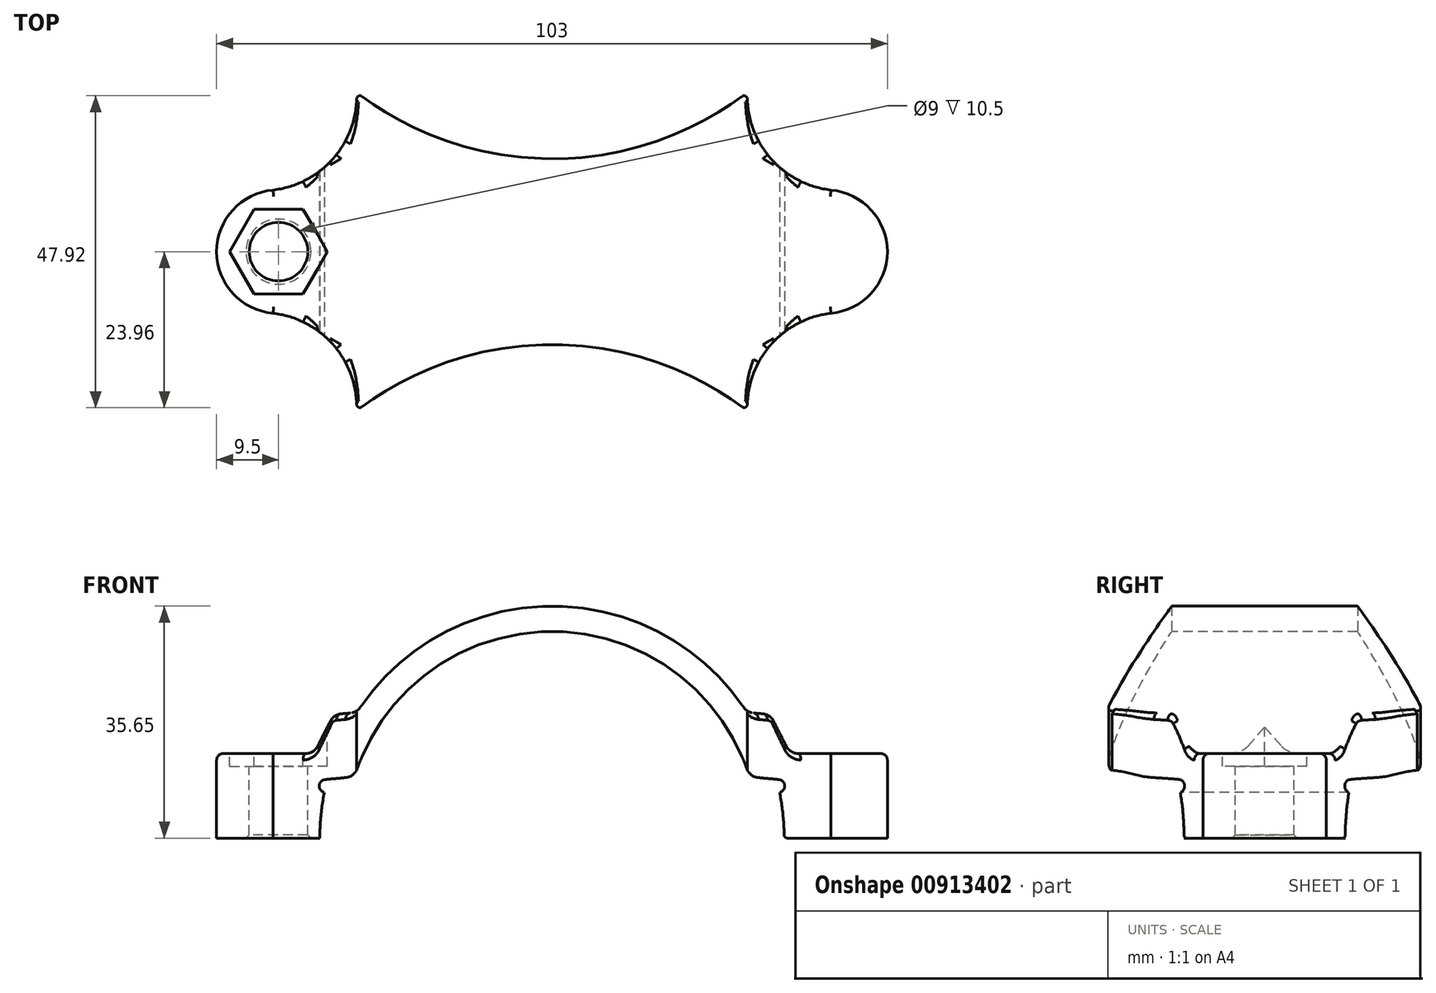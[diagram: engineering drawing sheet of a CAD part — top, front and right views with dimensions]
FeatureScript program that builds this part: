
annotation { "Feature Type Name" : "Feature", "Feature Type Description" : "" }
export const myFeature = defineFeature(function(context is Context, id is Id, definition is map)
    precondition{}
    {
        {
            var Q0;
            Q0=qCreatedBy(makeId("Top.planeOp"),FACE);
            var sketch = newSketch(context, id + "F0", { "sketchPlane" : qUnion([Q0])});
            skLineSegment(sketch, "E0", {"start": v(73.71, 0) * mm, "end": v(-77.72, 0) * mm, "construction": true});
            skLineSegment(sketch, "E1", {"start": v(0, 80.64) * mm, "end": v(0, -78.02) * mm, "construction": true});
            skLineSegment(sketch, "E2.0", {"start": v(42, 80.64) * mm, "end": v(42, -78.02) * mm, "construction": true});
            skArc(sketch, "E3", {"start": v(42.84, -9.46) * mm, "mid": v(51.5, 0) * mm, "end": v(42.84, 9.46) * mm});
            skLineSegment(sketch, "E4.0", {"start": v(29.5, 80.64) * mm, "end": v(29.5, -78.02) * mm, "construction": true});
            skArc(sketch, "E5", {"start": v(30, 23.46) * mm, "mid": v(29.73, 23.9) * mm, "end": v(29.2, 23.86) * mm});
            skPoint(sketch, "E6.first.point", {"position": v(30, 23.46) * mm});
            skArc(sketch, "E7.trimOffspring", {"start": v(30, 23.46) * mm, "mid": v(33.81, 14.06) * mm, "end": v(42.84, 9.46) * mm});
            skArc(sketch, "E8.MirrorCS", {"start": v(30, -23.46) * mm, "mid": v(33.81, -14.06) * mm, "end": v(42.84, -9.46) * mm});
            skArc(sketch, "E9.MirrorCS", {"start": v(30, -23.46) * mm, "mid": v(29.73, -23.9) * mm, "end": v(29.2, -23.86) * mm});
            skArc(sketch, "E10", {"start": v(-29.2, 23.86) * mm, "mid": v(0, 14.26) * mm, "end": v(29.2, 23.86) * mm});
            skArc(sketch, "E11.MirrorC", {"start": v(-29.2, -23.86) * mm, "mid": v(0, -14.26) * mm, "end": v(29.2, -23.86) * mm});
            skArc(sketch, "E12.MirrorCS", {"start": v(-30, 23.46) * mm, "mid": v(-29.73, 23.9) * mm, "end": v(-29.2, 23.86) * mm});
            skArc(sketch, "E13.MirrorCS", {"start": v(-30, 23.46) * mm, "mid": v(-33.81, 14.06) * mm, "end": v(-42.84, 9.46) * mm});
            skArc(sketch, "E14.MirrorC", {"start": v(-42.84, -9.46) * mm, "mid": v(-51.5, 0) * mm, "end": v(-42.84, 9.46) * mm});
            skArc(sketch, "E15.MirrorCS", {"start": v(-30, -23.46) * mm, "mid": v(-33.81, -14.06) * mm, "end": v(-42.84, -9.46) * mm});
            skArc(sketch, "E16.MirrorCS", {"start": v(-30, -23.46) * mm, "mid": v(-29.73, -23.9) * mm, "end": v(-29.2, -23.86) * mm});
            skPoint(sketch, "E17.orphan", {"position": v(29, -23.46) * mm});
            skPoint(sketch, "E18.orphan", {"position": v(-29, -23.46) * mm});
            skPoint(sketch, "E19.orphan", {"position": v(29, 23.46) * mm});
            skPoint(sketch, "E20.orphan", {"position": v(-29, 23.46) * mm});
            skSolve(sketch);
        }
        {
            var Q0;
            Q0=makeQuery(id+"F0.imprint","IMPRINT",FACE,{"disambiguationData":[TD([[makeQuery(id+"F0.imprint","IMPRINT",EDGE,{"derivedFrom":sQuery(id+"F0.wireOp",EDGE,"E3")}),1.0]])]});
            extrude(context, id + "F1", {"entities" : qUnion([Q0]), "depth" : 35.65 * mm, "offsetDistance" : 25 * mm});
        }
        {
            var Q0;
            Q0=qCreatedBy(makeId("Front.planeOp"),FACE);
            var sketch = newSketch(context, id + "F2", { "sketchPlane" : qUnion([Q0])});
            skLineSegment(sketch, "E21", {"start": v(75.28, 0) * mm, "end": v(-76.7, 0) * mm, "construction": true});
            skLineSegment(sketch, "E22", {"start": v(0, -8.46) * mm, "end": v(0, 103.78) * mm, "construction": true});
            skLineSegment(sketch, "E23.0", {"start": v(51.5, 13) * mm, "end": v(36.56, 13) * mm});
            skArc(sketch, "E24", {"start": v(30.32, 9.43) * mm, "mid": v(0, 31.75) * mm, "end": v(-30.32, 9.43) * mm});
            skArc(sketch, "E25", {"start": v(35.65, 0) * mm, "mid": v(35.47, 3.53) * mm, "end": v(34.95, 7.02) * mm});
            skLineSegment(sketch, "E26", {"start": v(33.5, 19) * mm, "end": v(29.97, 19.3) * mm});
            skLineSegment(sketch, "E27", {"start": v(33.5, 19) * mm, "end": v(36.56, 13) * mm});
            skLineSegment(sketch, "E28", {"start": v(51.5, 13) * mm, "end": v(51.5, 0) * mm});
            skLineSegment(sketch, "E29.0", {"start": v(75.28, 8) * mm, "end": v(-76.7, 8) * mm, "construction": true});
            skLineSegment(sketch, "E30.0", {"start": v(34.74, -8.46) * mm, "end": v(34.74, 103.78) * mm, "construction": true});
            skArc(sketch, "E31", {"start": v(34.95, 7.02) * mm, "mid": v(35.73, 8.1) * mm, "end": v(34.74, 9) * mm});
            skLineSegment(sketch, "E32.0", {"start": v(75.28, 9.43) * mm, "end": v(-76.7, 9.43) * mm, "construction": true});
            skLineSegment(sketch, "E33", {"start": v(30.32, 9.43) * mm, "end": v(34.84, 9) * mm});
            skArc(sketch, "E34.trimOffspring", {"start": v(29.97, 19.3) * mm, "mid": v(0, 35.65) * mm, "end": v(-29.97, 19.3) * mm});
            skArc(sketch, "E35.trimOffspring", {"start": v(34.74, 8) * mm, "mid": v(34.74, 8) * mm, "end": v(34.74, 8) * mm});
            skLineSegment(sketch, "E36", {"start": v(51.5, 13) * mm, "end": v(51.5, 42.22) * mm});
            skLineSegment(sketch, "E37", {"start": v(0, 35.65) * mm, "end": v(54.98, 35.65) * mm});
            skArc(sketch, "E38.MirrorCS", {"start": v(-35.65, 0) * mm, "mid": v(-35.47, 3.53) * mm, "end": v(-34.95, 7.02) * mm});
            skLineSegment(sketch, "E39.MirrorCS", {"start": v(-51.5, 13) * mm, "end": v(-51.5, 42.22) * mm});
            skLineSegment(sketch, "E40.MirrorCS", {"start": v(0, 35.65) * mm, "end": v(-54.98, 35.65) * mm});
            skArc(sketch, "E41.MirrorCS", {"start": v(-34.95, 7.02) * mm, "mid": v(-35.73, 8.1) * mm, "end": v(-34.74, 9) * mm});
            skLineSegment(sketch, "E42.MirrorCS", {"start": v(-30.32, 9.43) * mm, "end": v(-34.84, 9) * mm});
            skLineSegment(sketch, "E43.MirrorCS", {"start": v(-51.5, 13) * mm, "end": v(-51.5, 0) * mm});
            skLineSegment(sketch, "E44.MirrorCS", {"start": v(-51.5, 13) * mm, "end": v(-36.56, 13) * mm});
            skLineSegment(sketch, "E45.MirrorCS", {"start": v(-33.5, 19) * mm, "end": v(-36.56, 13) * mm});
            skLineSegment(sketch, "E46.MirrorCS", {"start": v(-33.5, 19) * mm, "end": v(-29.97, 19.3) * mm});
            skLineSegment(sketch, "E47", {"start": v(35.65, 0) * mm, "end": v(-35.65, 0) * mm});
            skSolve(sketch);
        }
        {
            var Q0;
            Q0=makeQuery(id+"F2.imprint","IMPRINT",FACE,{"disambiguationData":[TD([[makeQuery(id+"F2.imprint","IMPRINT",EDGE,{"derivedFrom":sQuery(id+"F2.wireOp",EDGE,"E24")}),1.0]])]});
            var Q1;
            {var subQ4=sQuery(id+"F2.wireOp",EDGE,"E23.0");Q1=makeQuery(id+"F2.imprint","IMPRINT",FACE,{"disambiguationData":[TD([[makeQuery(id+"F2.imprint","IMPRINT",EDGE,{"derivedFrom":subQ4}),-1.0]])]});}
            var Q2;
            {var subQ0=sQuery(id+"F2.wireOp",EDGE,"E44.MirrorCS");Q2=makeQuery(id+"F2.imprint","IMPRINT",FACE,{"disambiguationData":[TD([[makeQuery(id+"F2.imprint","IMPRINT",EDGE,{"derivedFrom":subQ0}),1.0]])]});}
            extrude(context, id + "F3", {"entities" : qUnion([Q0, Q1, Q2]), "operationType" : NewBodyOperationType.REMOVE, "endBound" : BoundingType.SYMMETRIC, "oppositeDirection" : true, "depth" : 50 * mm, "offsetDistance" : 25 * mm});
        }
        {
            var Q0;
            Q0=makeQuery(id+"F3.boolean.opBoolean","COPY",EDGE,{"derivedFrom":makeQuery(id+"F3.opExtrude","SWEPT_EDGE",EDGE,{"disambiguationData":[OSD([sQuery(id+"F2.wireOp",EDGE,"E24"),sQuery(id+"F2.wireOp",EDGE,"E42.MirrorCS")])]})});
            var Q1;
            Q1=makeQuery(id+"F3.boolean.opBoolean","COPY",EDGE,{"derivedFrom":makeQuery(id+"F3.opExtrude","SWEPT_EDGE",EDGE,{"disambiguationData":[OSD([sQuery(id+"F2.wireOp",EDGE,"E24"),sQuery(id+"F2.wireOp",EDGE,"E33")])]})});
            var Q2;
            Q2=makeQuery(id+"F3.boolean.opBoolean","COPY",EDGE,{"derivedFrom":makeQuery(id+"F3.opExtrude","SWEPT_EDGE",EDGE,{"disambiguationData":[OSD([sQuery(id+"F2.wireOp",EDGE,"E44.MirrorCS"),sQuery(id+"F2.wireOp",EDGE,"E45.MirrorCS")])]})});
            var Q3;
            Q3=makeQuery(id+"F3.boolean.opBoolean","COPY",EDGE,{"derivedFrom":makeQuery(id+"F3.opExtrude","SWEPT_EDGE",EDGE,{"disambiguationData":[OSD([sQuery(id+"F2.wireOp",EDGE,"E45.MirrorCS"),sQuery(id+"F2.wireOp",EDGE,"E46.MirrorCS")])]})});
            var Q4;
            Q4=makeQuery(id+"F3.boolean.opBoolean","COPY",EDGE,{"derivedFrom":makeQuery(id+"F3.opExtrude","SWEPT_EDGE",EDGE,{"disambiguationData":[OSD([sQuery(id+"F2.wireOp",EDGE,"E34.trimOffspring"),sQuery(id+"F2.wireOp",EDGE,"E46.MirrorCS")])]})});
            var Q5;
            Q5=makeQuery(id+"F3.boolean.opBoolean","COPY",EDGE,{"derivedFrom":makeQuery(id+"F3.opExtrude","SWEPT_EDGE",EDGE,{"disambiguationData":[OSD([sQuery(id+"F2.wireOp",EDGE,"E26"),sQuery(id+"F2.wireOp",EDGE,"E34.trimOffspring")])]})});
            var Q6;
            Q6=makeQuery(id+"F3.boolean.opBoolean","COPY",EDGE,{"derivedFrom":makeQuery(id+"F3.opExtrude","SWEPT_EDGE",EDGE,{"disambiguationData":[OSD([sQuery(id+"F2.wireOp",EDGE,"E26"),sQuery(id+"F2.wireOp",EDGE,"E27")])]})});
            var Q7;
            Q7=makeQuery(id+"F3.boolean.opBoolean","COPY",EDGE,{"derivedFrom":makeQuery(id+"F3.opExtrude","SWEPT_EDGE",EDGE,{"disambiguationData":[OSD([sQuery(id+"F2.wireOp",EDGE,"E23.0"),sQuery(id+"F2.wireOp",EDGE,"E27")])]})});
            fillet(context, id + "F4", {"entities" : qUnion([Q0, Q1, Q2, Q3, Q4, Q5, Q6, Q7]), "radius" : 2 * mm, "tangentPropagation" : true, "allowEdgeOverflow" : false});
        }
        {
            var Q0;
            Q0=makeQuery(id+"F3.boolean.opBoolean","COPY",EDGE,{"derivedFrom":makeQuery(id+"F3.opExtrude","SWEPT_EDGE",EDGE,{"disambiguationData":[OSD([sQuery(id+"F2.wireOp",EDGE,"E38.MirrorCS"),sQuery(id+"F2.wireOp",EDGE,"E47")])]})});
            var Q1;
            Q1=makeQuery(id+"F3.boolean.opBoolean","COPY",EDGE,{"derivedFrom":makeQuery(id+"F3.opExtrude","SWEPT_EDGE",EDGE,{"disambiguationData":[OSD([sQuery(id+"F2.wireOp",EDGE,"E25"),sQuery(id+"F2.wireOp",EDGE,"E47")])]})});
            fillet(context, id + "F5", {"entities" : qUnion([Q0, Q1]), "radius" : 0.5 * mm, "tangentPropagation" : true, "allowEdgeOverflow" : false});
        }
        {
            var Q0;
            Q0=makeQuery(id+"F3.boolean.opBoolean","COPY",FACE,{"derivedFrom":makeQuery(id+"F3.opExtrude","SWEPT_FACE",FACE,{"disambiguationData":[OSD([sQuery(id+"F2.wireOp",EDGE,"E23.0")])]})});
            var Q1;
            Q1=makeQuery(id+"F3.boolean.opBoolean","COPY",FACE,{"derivedFrom":makeQuery(id+"F3.opExtrude","SWEPT_FACE",FACE,{"disambiguationData":[OSD([sQuery(id+"F2.wireOp",EDGE,"E44.MirrorCS")])]})});
            fillet(context, id + "F6", {"entities" : qUnion([Q0, Q1]), "radius" : 1 * mm, "tangentPropagation" : true, "allowEdgeOverflow" : false});
        }
        {
            var Q0;
            Q0=makeQuery(id+"F3.boolean.opBoolean","COPY",FACE,{"derivedFrom":makeQuery(id+"F3.opExtrude","SWEPT_FACE",FACE,{"disambiguationData":[OSD([sQuery(id+"F2.wireOp",EDGE,"E44.MirrorCS")])]})});
            var sketch = newSketch(context, id + "F7", { "sketchPlane" : qUnion([Q0])});
            skLineSegment(sketch, "E48", {"start": v(-56.2, 0) * mm, "end": v(-26.03, 0) * mm, "construction": true});
            skCircle(sketch, "E49", {"center": v(-42, 0) * mm, "radius": 4.5 * mm});
            skCircle(sketch, "E50.cCircle", {"center": v(-42, 0) * mm, "radius": 6.5 * mm, "construction": true});
            skLineSegment(sketch, "E50.0", {"start": v(-45.75, -6.5) * mm, "end": v(-49.5, 0) * mm});
            skLineSegment(sketch, "E50.1", {"start": v(-49.5, 0) * mm, "end": v(-45.75, 6.5) * mm});
            skLineSegment(sketch, "E50.2", {"start": v(-45.75, 6.5) * mm, "end": v(-38.25, 6.5) * mm});
            skLineSegment(sketch, "E50.3", {"start": v(-38.25, 6.5) * mm, "end": v(-34.5, 0) * mm});
            skLineSegment(sketch, "E50.4", {"start": v(-34.5, 0) * mm, "end": v(-38.25, -6.5) * mm});
            skLineSegment(sketch, "E50.5", {"start": v(-38.25, -6.5) * mm, "end": v(-45.75, -6.5) * mm});
            skPoint(sketch, "E50.0.midPoint", {"position": v(-47.63, -3.25) * mm});
            skSolve(sketch);
        }
        {
            var Q0;
            Q0=makeQuery(id+"F7.imprint","IMPRINT",FACE,{"disambiguationData":[TD([[makeQuery(id+"F7.imprint","IMPRINT",EDGE,{"derivedFrom":sQuery(id+"F7.wireOp",EDGE,"E50.0")}),-1.0]])]});
            var Q1;
            {var subQ0=sQuery(id+"F7.wireOp",EDGE,"E50.3");var subQ6=sQuery(id+"F7.wireOp",EDGE,"E50.4");var subQ7=makeQuery(id+"F7.imprint","INTERSECT",VERTEX,{"derivedFrom":[subQ0,subQ6]});Q1=makeQuery(id+"F7.imprint","IMPRINT",FACE,{"disambiguationData":[TD([[makeQuery(id+"F7.imprint","IMPRINT",EDGE,{"disambiguationData":[TD([[subQ7,1.0]])],"derivedFrom":subQ0}),-1.0]])]});}
            var Q2;
            {var subQ0=sQuery(id+"F7.wireOp",EDGE,"E49");var subQ1=sQuery(id+"F2.wireOp",EDGE,"E44.MirrorCS");var subQ2=makeQuery(id+"F4.opFillet","BLEND_EDGE",EDGE,{"blendedFrom":[makeQuery(id+"F3.boolean.opBoolean","COPY",EDGE,{"derivedFrom":makeQuery(id+"F3.opExtrude","SWEPT_EDGE",EDGE,{"disambiguationData":[OSD([subQ1,sQuery(id+"F2.wireOp",EDGE,"E45.MirrorCS")])]})}),makeQuery(id+"F3.boolean.opBoolean","COPY",FACE,{"derivedFrom":makeQuery(id+"F3.opExtrude","SWEPT_FACE",FACE,{"disambiguationData":[OSD([subQ1])]})})],"blendedInto":[makeQuery(id+"F3.boolean.opBoolean","COPY",FACE,{"derivedFrom":makeQuery(id+"F3.opExtrude","SWEPT_FACE",FACE,{"disambiguationData":[OSD([subQ1])]})})]});var subQ3=makeQuery(id+"F7.imprint","INTERSECT",VERTEX,{"disambiguationData":[OD(0.0)],"derivedFrom":[subQ2,subQ0]});Q2=makeQuery(id+"F7.imprint","IMPRINT",FACE,{"disambiguationData":[TD([[makeQuery(id+"F7.imprint","IMPRINT",EDGE,{"disambiguationData":[TD([[subQ3,-1.0]])],"derivedFrom":subQ0}),1.0]])]});}
            var Q3;
            {var subQ0=sQuery(id+"F7.wireOp",EDGE,"E49");var subQ1=sQuery(id+"F2.wireOp",EDGE,"E44.MirrorCS");var subQ2=makeQuery(id+"F4.opFillet","BLEND_EDGE",EDGE,{"blendedFrom":[makeQuery(id+"F3.boolean.opBoolean","COPY",EDGE,{"derivedFrom":makeQuery(id+"F3.opExtrude","SWEPT_EDGE",EDGE,{"disambiguationData":[OSD([subQ1,sQuery(id+"F2.wireOp",EDGE,"E45.MirrorCS")])]})}),makeQuery(id+"F3.boolean.opBoolean","COPY",FACE,{"derivedFrom":makeQuery(id+"F3.opExtrude","SWEPT_FACE",FACE,{"disambiguationData":[OSD([subQ1])]})})],"blendedInto":[makeQuery(id+"F3.boolean.opBoolean","COPY",FACE,{"derivedFrom":makeQuery(id+"F3.opExtrude","SWEPT_FACE",FACE,{"disambiguationData":[OSD([subQ1])]})})]});var subQ3=makeQuery(id+"F7.imprint","INTERSECT",VERTEX,{"disambiguationData":[OD(0.0)],"derivedFrom":[subQ2,subQ0]});Q3=makeQuery(id+"F7.imprint","IMPRINT",FACE,{"disambiguationData":[TD([[makeQuery(id+"F7.imprint","IMPRINT",EDGE,{"disambiguationData":[TD([[subQ3,1.0]])],"derivedFrom":subQ0}),1.0]])]});}
            extrude(context, id + "F8", {"entities" : qUnion([Q0, Q1, Q2, Q3]), "operationType" : NewBodyOperationType.REMOVE, "oppositeDirection" : true, "depth" : 2 * mm, "offsetDistance" : 25 * mm});
        }
        {
            var Q0;
            Q0=makeQuery(id+"F8.boolean.opBoolean","COPY",FACE,{"derivedFrom":makeQuery(id+"F8.opExtrude","CAP_FACE",FACE,{"disambiguationData":[OSD([sQuery(id+"F7.wireOp",EDGE,"E50.0"),sQuery(id+"F7.wireOp",EDGE,"E50.1"),sQuery(id+"F7.wireOp",EDGE,"E50.2"),sQuery(id+"F7.wireOp",EDGE,"E50.3"),sQuery(id+"F7.wireOp",EDGE,"E50.4"),sQuery(id+"F7.wireOp",EDGE,"E50.5")])],"isStart":false})});
            extrude(context, id + "F9", {"entities" : qUnion([Q0]), "operationType" : NewBodyOperationType.REMOVE, "depth" : 25 * mm, "offsetDistance" : 25 * mm});
        }
        {
            var Q0;
            {var subQ0=sQuery(id+"F7.wireOp",EDGE,"E49");var subQ1=sQuery(id+"F2.wireOp",EDGE,"E44.MirrorCS");var subQ2=makeQuery(id+"F4.opFillet","BLEND_EDGE",EDGE,{"blendedFrom":[makeQuery(id+"F3.boolean.opBoolean","COPY",EDGE,{"derivedFrom":makeQuery(id+"F3.opExtrude","SWEPT_EDGE",EDGE,{"disambiguationData":[OSD([subQ1,sQuery(id+"F2.wireOp",EDGE,"E45.MirrorCS")])]})}),makeQuery(id+"F3.boolean.opBoolean","COPY",FACE,{"derivedFrom":makeQuery(id+"F3.opExtrude","SWEPT_FACE",FACE,{"disambiguationData":[OSD([subQ1])]})})],"blendedInto":[makeQuery(id+"F3.boolean.opBoolean","COPY",FACE,{"derivedFrom":makeQuery(id+"F3.opExtrude","SWEPT_FACE",FACE,{"disambiguationData":[OSD([subQ1])]})})]});var subQ3=makeQuery(id+"F7.imprint","INTERSECT",VERTEX,{"disambiguationData":[OD(0.0)],"derivedFrom":[subQ2,subQ0]});Q0=makeQuery(id+"F7.imprint","IMPRINT",FACE,{"disambiguationData":[TD([[makeQuery(id+"F7.imprint","IMPRINT",EDGE,{"disambiguationData":[TD([[subQ3,-1.0]])],"derivedFrom":subQ0}),1.0]])]});}
            var Q1;
            {var subQ0=sQuery(id+"F7.wireOp",EDGE,"E49");var subQ1=sQuery(id+"F2.wireOp",EDGE,"E44.MirrorCS");var subQ2=makeQuery(id+"F4.opFillet","BLEND_EDGE",EDGE,{"blendedFrom":[makeQuery(id+"F3.boolean.opBoolean","COPY",EDGE,{"derivedFrom":makeQuery(id+"F3.opExtrude","SWEPT_EDGE",EDGE,{"disambiguationData":[OSD([subQ1,sQuery(id+"F2.wireOp",EDGE,"E45.MirrorCS")])]})}),makeQuery(id+"F3.boolean.opBoolean","COPY",FACE,{"derivedFrom":makeQuery(id+"F3.opExtrude","SWEPT_FACE",FACE,{"disambiguationData":[OSD([subQ1])]})})],"blendedInto":[makeQuery(id+"F3.boolean.opBoolean","COPY",FACE,{"derivedFrom":makeQuery(id+"F3.opExtrude","SWEPT_FACE",FACE,{"disambiguationData":[OSD([subQ1])]})})]});var subQ3=makeQuery(id+"F7.imprint","INTERSECT",VERTEX,{"disambiguationData":[OD(0.0)],"derivedFrom":[subQ2,subQ0]});Q1=makeQuery(id+"F7.imprint","IMPRINT",FACE,{"disambiguationData":[TD([[makeQuery(id+"F7.imprint","IMPRINT",EDGE,{"disambiguationData":[TD([[subQ3,1.0]])],"derivedFrom":subQ0}),1.0]])]});}
            extrude(context, id + "F10", {"entities" : qUnion([Q0, Q1]), "operationType" : NewBodyOperationType.REMOVE, "oppositeDirection" : true, "depth" : 25 * mm, "offsetDistance" : 25 * mm});
        }
        {
            var Q0;
            {var subQ0=sQuery(id+"F0.wireOp",EDGE,"E3");var subQ1=sQuery(id+"F0.wireOp",EDGE,"E8.MirrorCS");var subQ2=sQuery(id+"F0.wireOp",EDGE,"E7.trimOffspring");Q0=makeQuery(id+"FTqmAWbSo514EAX_1.1.F10.boolean.opBoolean","INTERSECT",EDGE,{"derivedFrom":[makeQuery(id+"F3.boolean.opBoolean","SPLIT",FACE,{"disambiguationData":[TD([makeQuery(id+"F1.opExtrude","SWEPT_FACE",FACE,{"disambiguationData":[OSD([subQ0])]})])],"derivedFrom":makeQuery(id+"F1.opExtrude","CAP_FACE",FACE,{"disambiguationData":[OSD([subQ0,sQuery(id+"F0.wireOp",EDGE,"E5"),subQ2,subQ1,sQuery(id+"F0.wireOp",EDGE,"E9.MirrorCS"),sQuery(id+"F0.wireOp",EDGE,"E10"),sQuery(id+"F0.wireOp",EDGE,"E11.MirrorC"),sQuery(id+"F0.wireOp",EDGE,"E12.MirrorCS"),sQuery(id+"F0.wireOp",EDGE,"E13.MirrorCS"),sQuery(id+"F0.wireOp",EDGE,"E14.MirrorC"),sQuery(id+"F0.wireOp",EDGE,"E15.MirrorCS"),sQuery(id+"F0.wireOp",EDGE,"E16.MirrorCS")])],"isStart":true})}),makeQuery(id+"FTqmAWbSo514EAX_1.1.F10.opExtrude","SWEPT_FACE",FACE,{"disambiguationData":[OSD([sQuery(id+"F7.wireOp",EDGE,"E49")])]})]});}
            var Q1;
            {var subQ0=sQuery(id+"F0.wireOp",EDGE,"E13.MirrorCS");var subQ1=sQuery(id+"F0.wireOp",EDGE,"E14.MirrorC");var subQ2=sQuery(id+"F0.wireOp",EDGE,"E15.MirrorCS");Q1=makeQuery(id+"F10.boolean.opBoolean","INTERSECT",EDGE,{"derivedFrom":[makeQuery(id+"F3.boolean.opBoolean","SPLIT",FACE,{"disambiguationData":[TD([makeQuery(id+"F1.opExtrude","SWEPT_FACE",FACE,{"disambiguationData":[OSD([subQ0])]})])],"derivedFrom":makeQuery(id+"F1.opExtrude","CAP_FACE",FACE,{"disambiguationData":[OSD([sQuery(id+"F0.wireOp",EDGE,"E3"),sQuery(id+"F0.wireOp",EDGE,"E5"),sQuery(id+"F0.wireOp",EDGE,"E7.trimOffspring"),sQuery(id+"F0.wireOp",EDGE,"E8.MirrorCS"),sQuery(id+"F0.wireOp",EDGE,"E9.MirrorCS"),sQuery(id+"F0.wireOp",EDGE,"E10"),sQuery(id+"F0.wireOp",EDGE,"E11.MirrorC"),sQuery(id+"F0.wireOp",EDGE,"E12.MirrorCS"),subQ0,subQ1,subQ2,sQuery(id+"F0.wireOp",EDGE,"E16.MirrorCS")])],"isStart":true})}),makeQuery(id+"F10.opExtrude","SWEPT_FACE",FACE,{"disambiguationData":[OSD([sQuery(id+"F7.wireOp",EDGE,"E49")])]})]});}
            chamfer(context, id + "F11", {"entities" : qUnion([Q0, Q1]), "width" : 0.5 * mm, "tangentPropagation" : true});
        }
    });
